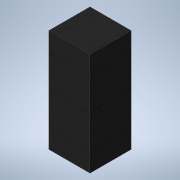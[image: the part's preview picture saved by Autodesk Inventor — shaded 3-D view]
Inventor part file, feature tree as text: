
AUTODESK INVENTOR PART (.ipt)
format: ipt  version: 2022 (Build 260153000, 153)  size: 101,376 bytes
history: native  units: in
note: dims shown in document units (in); Inventor stores cm internally (conversion verified against a paired STEP export)
features: other x1, extrude x1, sketch x1
ambient origin geometry x8: Origin, YZ Plane, XZ Plane, XY Plane, X Axis, Y Axis, Z Axis, Center Point
bodies: Solid1 (feature_tree)
feature tree (3):
  other  "ElectronicsRack"
  extrude  "Extrusion1"  Depth=24.0in
  sketch  "Sketch1"  dims[d0=24.0in d1=24.0in d2=60.0in d3=0.0in]
